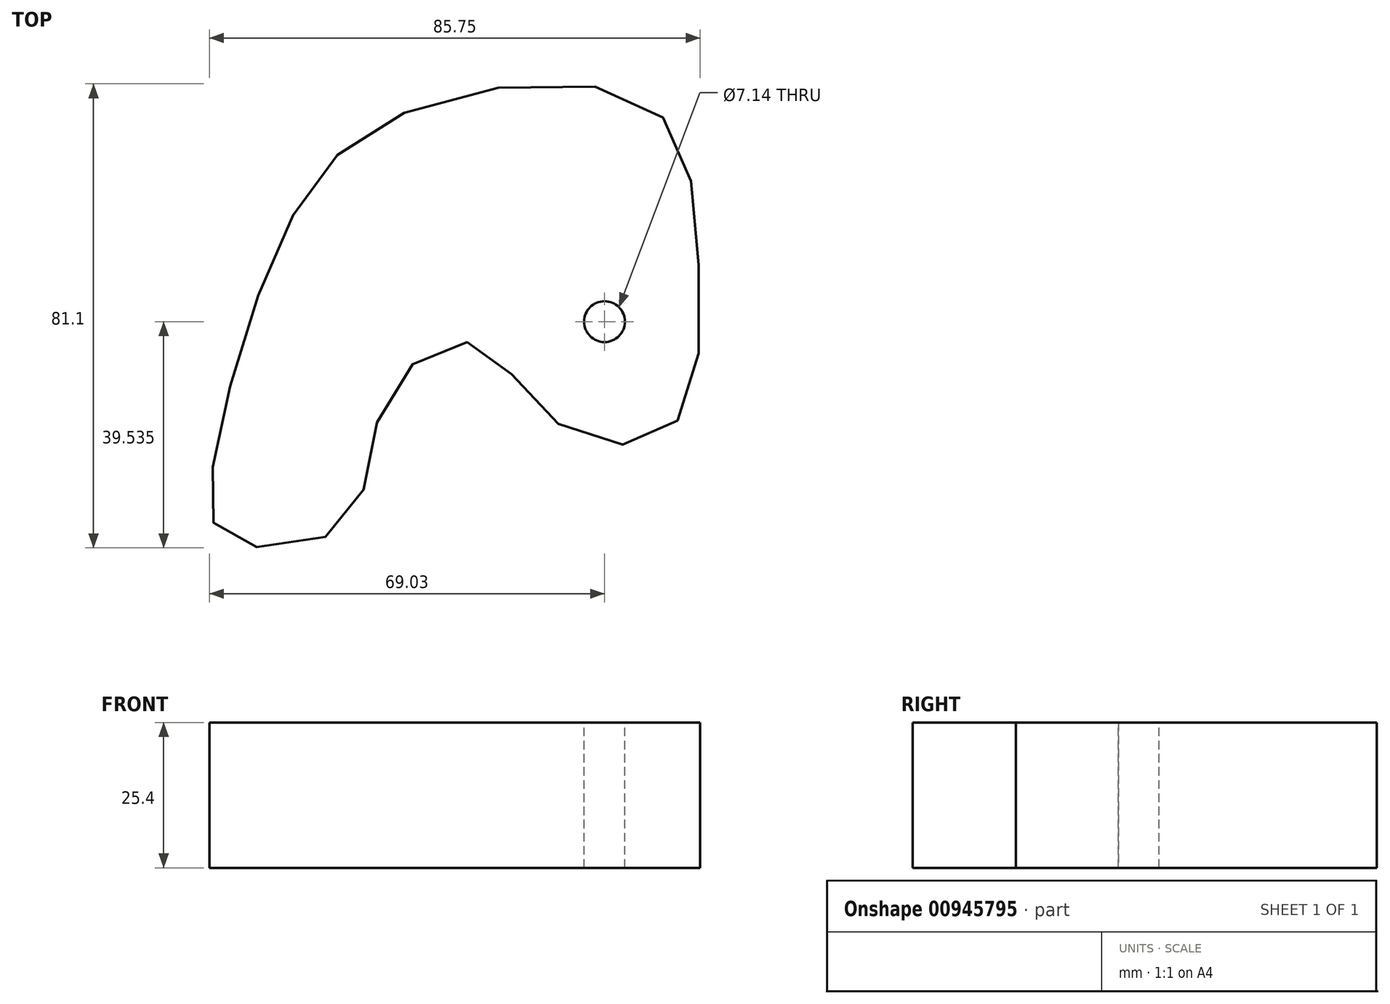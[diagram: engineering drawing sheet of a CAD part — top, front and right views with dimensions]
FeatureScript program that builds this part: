
annotation { "Feature Type Name" : "Feature", "Feature Type Description" : "" }
export const myFeature = defineFeature(function(context is Context, id is Id, definition is map)
    precondition{}
    {
        {
            var Q0;
            Q0=qCreatedBy(makeId("Top.planeOp"),FACE);
            var sketch = newSketch(context, id + "F0", { "sketchPlane" : qUnion([Q0])});
            skFitSpline(sketch, "E0", {"points": [v(-42.4, -30.24) * mm, v(-30.43, 9.57) * mm, v(-9.57, 31.38) * mm, v(33.27, 33.27) * mm, v(42.37, 7.49) * mm, v(37.64, -23.42) * mm, v(17.92, -22.66) * mm, v(3.13, -8.63) * mm, v(-12.23, -18.49) * mm, v(-19.24, -40.1) * mm, v(-39.72, -42.75) * mm, v(-42.4, -30.24) * mm]});
            skSolve(sketch);
        }
        {
            var Q0;
            Q0 = qSketchRegion(id + "F0", true);
            extrude(context, id + "F1", {"entities" : qUnion([Q0]), "depth" : 25.4 * mm, "offsetDistance" : 25.4 * mm});
        }
        {
            var Q0;
            Q0=makeQuery(id+"F1.opExtrude","CAP_FACE",FACE,{"disambiguationData":[OSD([sQuery(id+"F0.wireOp",EDGE,"E0")])],"isStart":false});
            var sketch = newSketch(context, id + "F2", { "sketchPlane" : qUnion([Q0])});
            skPoint(sketch, "E1", {"position": v(26.07, -4.83) * mm});
            skSolve(sketch);
        }
        {
            var Q0;
            Q0=sQuery(id+"F2.wireOp",VERTEX,"E1");
            var Q1;
            Q1=makeQuery(id+"F1.opExtrude","SWEPT_BODY",BODY,{"disambiguationData":[OSD([sQuery(id+"F0.wireOp",EDGE,"E0")])]});
            hole(context, id + "F3", {"style" : HoleStyle.SIMPLE, "endStyle" : HoleEndStyle.THROUGH, "standardTappedOrClearance" : lookupTablePath({ "fit" : "Normal (ASME)", "standard" : "ANSI", "size" : "1/4", "type" : "Clearance" }), "standardBlindInLast" : lookupTablePath({ "fit" : "Normal", "standard" : "ANSI", "engagement" : "75%", "pitch" : "20 tpi", "size" : "1/4", "type" : "Clearance & tapped" }), "holeDiameter" : 7.14 * mm, "majorDiameter" : 6.35 * mm, "isTappedThrough" : true, "tappedDepth" : 12.7 * mm, "tapClearance" : 3, "locations" : qUnion([Q0]), "scope" : qUnion([Q1])});
        }
    });
